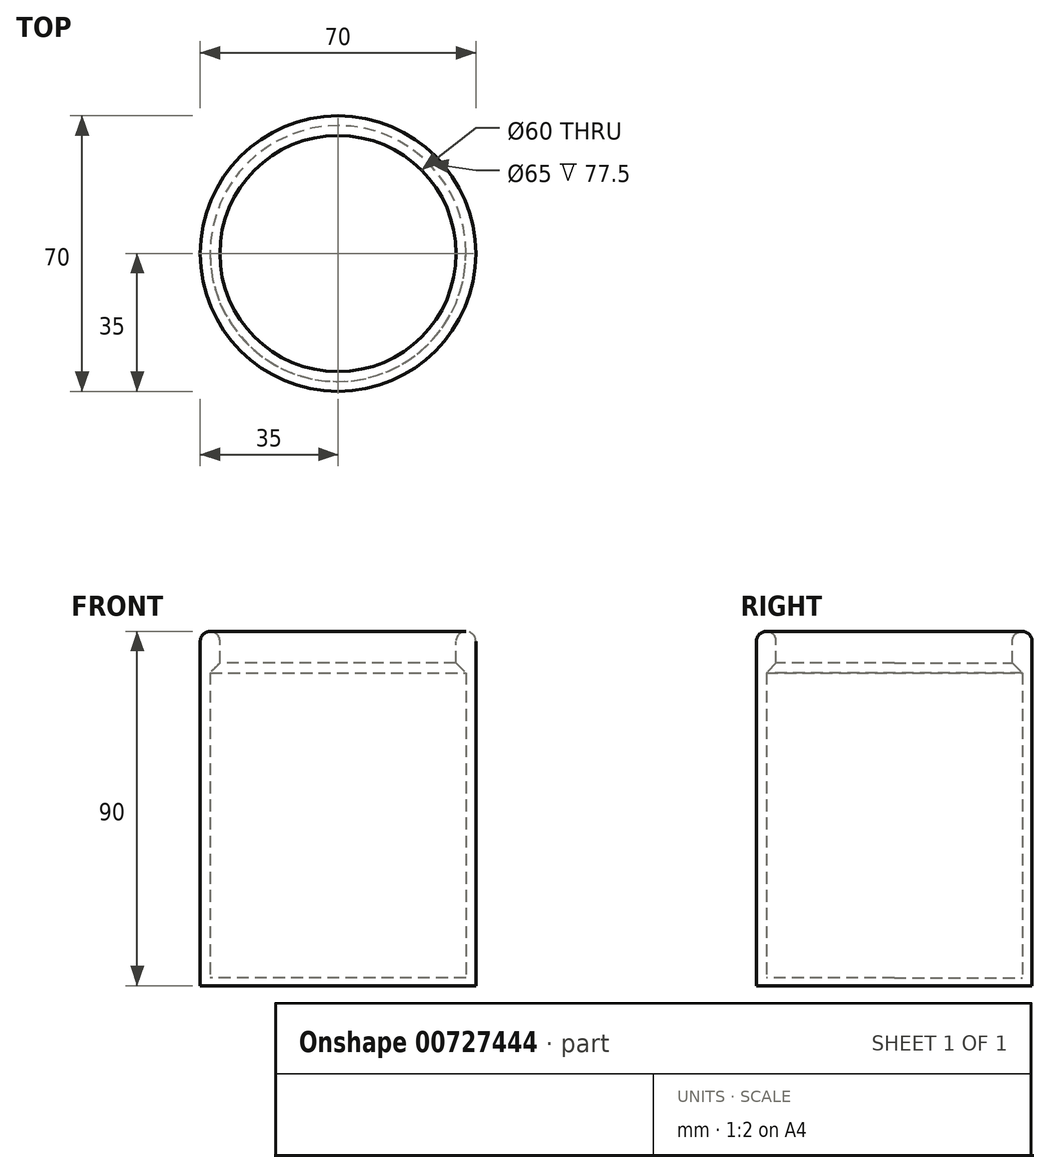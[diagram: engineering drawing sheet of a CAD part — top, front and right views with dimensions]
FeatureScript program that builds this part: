
annotation { "Feature Type Name" : "Feature", "Feature Type Description" : "" }
export const myFeature = defineFeature(function(context is Context, id is Id, definition is map)
    precondition{}
    {
        {
            var Q0;
            Q0=qCreatedBy(makeId("Top.planeOp"),FACE);
            var sketch = newSketch(context, id + "F0", { "sketchPlane" : qUnion([Q0])});
            skCircle(sketch, "E0", {"center": v(0, 0) * mm, "radius": 35 * mm});
            skCircle(sketch, "E1", {"center": v(0, 0) * mm, "radius": 32.5 * mm});
            skLineSegment(sketch, "E2", {"start": v(0, 0) * mm, "end": v(0, 50) * mm});
            skCircle(sketch, "E3", {"center": v(0, 50) * mm, "radius": 15 * mm});
            skSolve(sketch);
        }
        {
            var Q0;
            Q0=makeQuery(id+"F0.imprint","IMPRINT",FACE,{"disambiguationData":[TD([[makeQuery(id+"F0.imprint","IMPRINT",EDGE,{"derivedFrom":sQuery(id+"F0.wireOp",EDGE,"E0")}),1.0]])]});
            extrude(context, id + "F1", {"entities" : qUnion([Q0]), "depth" : 90 * mm, "offsetDistance" : 25 * mm});
        }
        {
            var Q0;
            Q0=makeQuery(id+"F1.opExtrude","CAP_FACE",FACE,{"disambiguationData":[OSD([sQuery(id+"F0.wireOp",EDGE,"E0"),sQuery(id+"F0.wireOp",EDGE,"E1")])],"isStart":false});
            var sketch = newSketch(context, id + "F2", { "sketchPlane" : qUnion([Q0])});
            skCircle(sketch, "E4", {"center": v(0, 0) * mm, "radius": 32.5 * mm});
            skCircle(sketch, "E5", {"center": v(0, 0) * mm, "radius": 30 * mm});
            skSolve(sketch);
        }
        {
            var Q0;
            Q0=makeQuery(id+"F2.imprint","IMPRINT",FACE,{"disambiguationData":[TD([[makeQuery(id+"F2.imprint","IMPRINT",EDGE,{"derivedFrom":sQuery(id+"F2.wireOp",EDGE,"E4")}),1.0]])]});
            extrude(context, id + "F3", {"entities" : qUnion([Q0]), "operationType" : NewBodyOperationType.ADD, "oppositeDirection" : true, "depth" : 3 * mm, "offsetDistance" : 25 * mm});
        }
        {
            var Q0;
            Q0=makeQuery(id+"F0.imprint","IMPRINT",FACE,{"disambiguationData":[TD([[makeQuery(id+"F0.imprint","IMPRINT",EDGE,{"derivedFrom":sQuery(id+"F0.wireOp",EDGE,"E1")}),1.0]])]});
            extrude(context, id + "F4", {"entities" : qUnion([Q0]), "operationType" : NewBodyOperationType.ADD, "depth" : 2 * mm, "offsetDistance" : 25 * mm});
        }
        {
            var Q0;
            Q0=makeQuery(id+"F3.opExtrude","CAP_FACE",FACE,{"disambiguationData":[OSD([sQuery(id+"F2.wireOp",EDGE,"E4"),sQuery(id+"F2.wireOp",EDGE,"E5")])],"isStart":false});
            extrude(context, id + "F5", {"entities" : qUnion([Q0]), "operationType" : NewBodyOperationType.ADD, "depth" : 10 * mm, "offsetDistance" : 25 * mm});
        }
        {
            var Q0;
            Q0=makeQuery(id+"F5.opExtrude","CAP_EDGE",EDGE,{"disambiguationData":[OSD([sQuery(id+"F2.wireOp",EDGE,"E5")])],"isStart":false});
            chamfer(context, id + "F6", {"entities" : qUnion([Q0]), "width" : 5 * mm, "tangentPropagation" : true});
        }
        {
            var Q0;
            Q0=makeQuery(id+"F3.opExtrude","CAP_EDGE",EDGE,{"disambiguationData":[OSD([sQuery(id+"F2.wireOp",EDGE,"E5")])],"isStart":true});
            var Q1;
            Q1=makeQuery(id+"F1.opExtrude","CAP_EDGE",EDGE,{"disambiguationData":[OSD([sQuery(id+"F0.wireOp",EDGE,"E0")])],"isStart":false});
            fillet(context, id + "F7", {"entities" : qUnion([Q0, Q1]), "radius" : 2.5 * mm, "tangentPropagation" : true, "defaultsChanged" : false, "vertexSettings" : [], "allowEdgeOverflow" : false});
        }
    });
